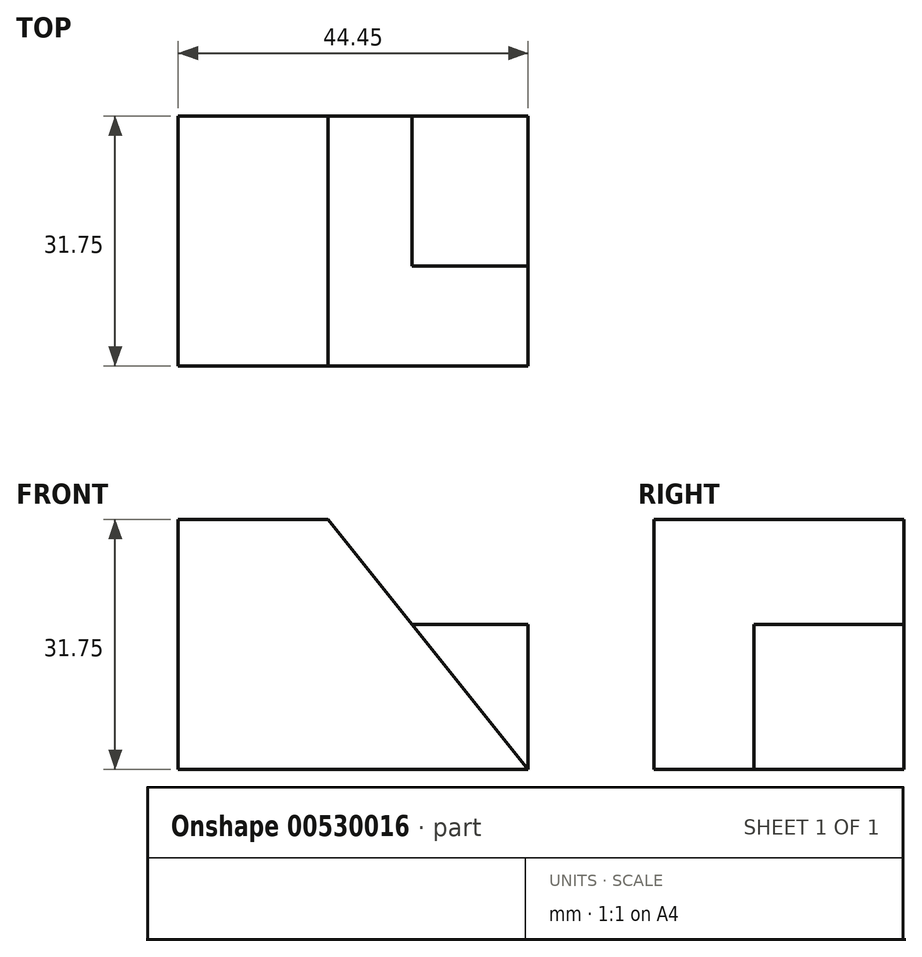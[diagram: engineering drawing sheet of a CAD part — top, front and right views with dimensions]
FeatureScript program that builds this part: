
annotation { "Feature Type Name" : "Feature", "Feature Type Description" : "" }
export const myFeature = defineFeature(function(context is Context, id is Id, definition is map)
    precondition{}
    {
        {
            var Q0;
            Q0=qCreatedBy(makeId("Front.planeOp"),FACE);
            var sketch = newSketch(context, id + "F0", { "sketchPlane" : qUnion([Q0])});
            skLineSegment(sketch, "E0", {"start": v(-57.97, 51.47) * mm, "end": v(-57.97, 19.72) * mm});
            skLineSegment(sketch, "E1", {"start": v(-57.97, 51.47) * mm, "end": v(-13.52, 51.47) * mm});
            skLineSegment(sketch, "E2", {"start": v(-13.52, 51.47) * mm, "end": v(-13.52, 19.72) * mm});
            skLineSegment(sketch, "E3", {"start": v(-57.97, 19.72) * mm, "end": v(-13.52, 19.72) * mm});
            skSolve(sketch);
        }
        {
            var Q0;
            Q0=makeQuery(id+"F0.imprint","IMPRINT",FACE,{"disambiguationData":[TD([[makeQuery(id+"F0.imprint","IMPRINT",EDGE,{"derivedFrom":sQuery(id+"F0.wireOp",EDGE,"E0")}),1.0]])]});
            extrude(context, id + "F1", {"entities" : qUnion([Q0]), "depth" : 31.75 * mm, "offsetDistance" : 25.4 * mm});
        }
        {
            var Q0;
            Q0=makeQuery(id+"F1.opExtrude","CAP_FACE",FACE,{"disambiguationData":[OSD([sQuery(id+"F0.wireOp",EDGE,"E0"),sQuery(id+"F0.wireOp",EDGE,"E1"),sQuery(id+"F0.wireOp",EDGE,"E2"),sQuery(id+"F0.wireOp",EDGE,"E3")])],"isStart":false});
            var sketch = newSketch(context, id + "F2", { "sketchPlane" : qUnion([Q0])});
            skLineSegment(sketch, "E4", {"start": v(-13.52, 19.72) * mm, "end": v(-38.92, 51.47) * mm});
            skLineSegment(sketch, "E5", {"start": v(-38.92, 51.47) * mm, "end": v(-13.52, 51.47) * mm});
            skLineSegment(sketch, "E6", {"start": v(-13.52, 51.47) * mm, "end": v(-13.52, 19.72) * mm});
            skSolve(sketch);
        }
        {
            var Q0;
            Q0=makeQuery(id+"F2.imprint","IMPRINT",FACE,{"disambiguationData":[TD([[makeQuery(id+"F2.imprint","IMPRINT",EDGE,{"derivedFrom":sQuery(id+"F2.wireOp",EDGE,"E4")}),-1.0]])]});
            extrude(context, id + "F3", {"entities" : qUnion([Q0]), "operationType" : NewBodyOperationType.REMOVE, "oppositeDirection" : true, "depth" : 12.7 * mm, "offsetDistance" : 25.4 * mm});
        }
        {
            var Q0;
            Q0=makeQuery(id+"F3.boolean.opBoolean","COPY",FACE,{"derivedFrom":makeQuery(id+"F3.opExtrude","CAP_FACE",FACE,{"disambiguationData":[OSD([sQuery(id+"F2.wireOp",EDGE,"E4"),sQuery(id+"F2.wireOp",EDGE,"E5"),sQuery(id+"F2.wireOp",EDGE,"E6")])],"isStart":false})});
            var sketch = newSketch(context, id + "F4", { "sketchPlane" : qUnion([Q0])});
            skLineSegment(sketch, "E7", {"start": v(-38.92, 51.47) * mm, "end": v(-28.25, 38.13) * mm});
            skLineSegment(sketch, "E8", {"start": v(-28.25, 38.13) * mm, "end": v(-13.52, 38.13) * mm});
            skLineSegment(sketch, "E9", {"start": v(-38.92, 51.47) * mm, "end": v(-13.52, 51.47) * mm});
            skLineSegment(sketch, "E10", {"start": v(-13.52, 51.47) * mm, "end": v(-13.52, 38.13) * mm});
            skSolve(sketch);
        }
        {
            var Q0;
            Q0=makeQuery(id+"F4.imprint","IMPRINT",FACE,{"disambiguationData":[TD([[makeQuery(id+"F4.imprint","IMPRINT",EDGE,{"derivedFrom":sQuery(id+"F4.wireOp",EDGE,"E7")}),-1.0]])]});
            extrude(context, id + "F5", {"entities" : qUnion([Q0]), "operationType" : NewBodyOperationType.REMOVE, "endBound" : BoundingType.THROUGH_ALL, "oppositeDirection" : true, "depth" : 25.4 * mm, "offsetDistance" : 25.4 * mm});
        }
    });
